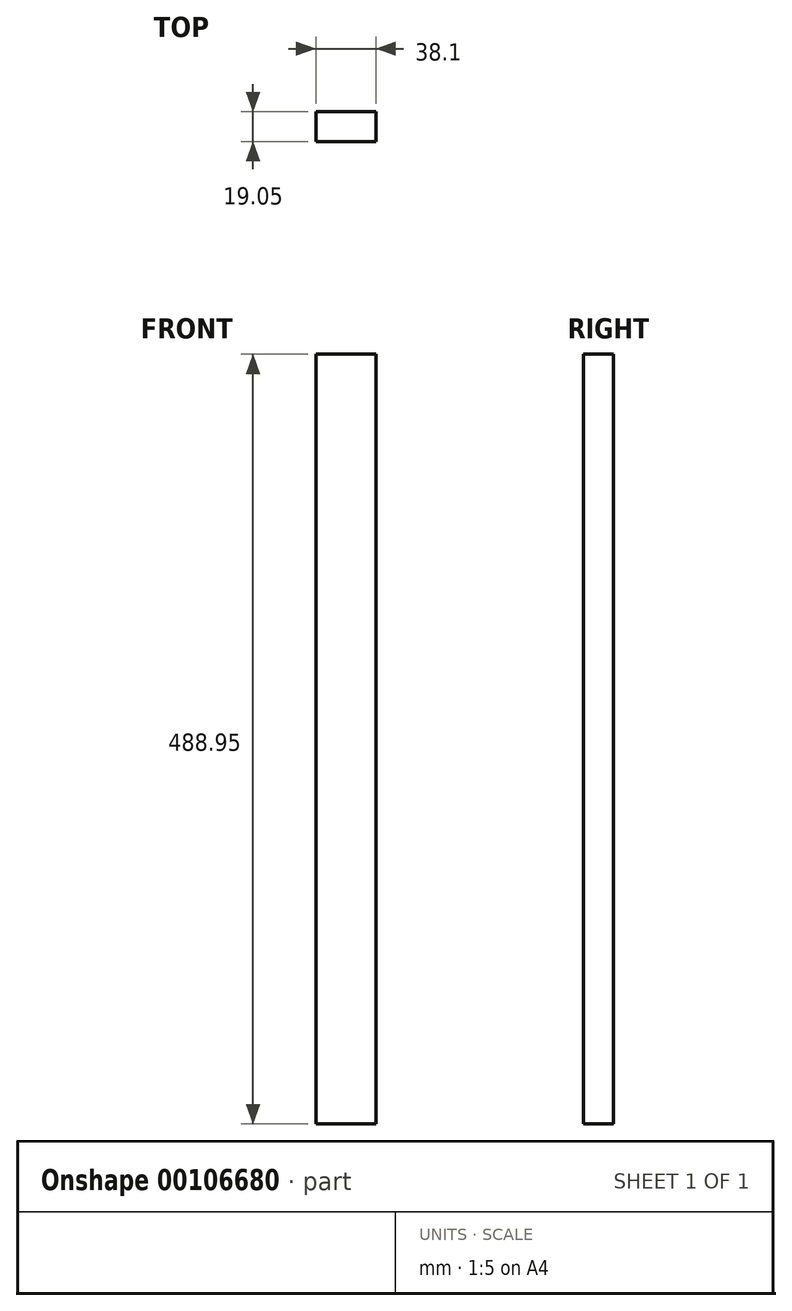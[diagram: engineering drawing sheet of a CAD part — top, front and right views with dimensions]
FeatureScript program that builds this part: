
annotation { "Feature Type Name" : "Feature", "Feature Type Description" : "" }
export const myFeature = defineFeature(function(context is Context, id is Id, definition is map)
    precondition{}
    {
        {
            var Q0;
            Q0=qCreatedBy(makeId("Front.planeOp"),FACE);
            var sketch = newSketch(context, id + "F0", { "sketchPlane" : qUnion([Q0])});
            skLineSegment(sketch, "E0.bottom", {"start": v(0, 0) * mm, "end": v(38.1, 0) * mm});
            skLineSegment(sketch, "E0.left", {"start": v(0, 0) * mm, "end": v(0, 488.95) * mm});
            skLineSegment(sketch, "E0.right", {"start": v(38.1, 0) * mm, "end": v(38.1, 488.95) * mm});
            skLineSegment(sketch, "E1", {"start": v(0, 488.95) * mm, "end": v(38.1, 488.95) * mm});
            skSolve(sketch);
        }
        {
            var Q0;
            Q0=makeQuery(id+"F0.imprint","IMPRINT",FACE,{"disambiguationData":[TD([[makeQuery(id+"F0.imprint","IMPRINT",EDGE,{"derivedFrom":sQuery(id+"F0.wireOp",EDGE,"E0.bottom")}),1.0]])]});
            extrude(context, id + "F1", {"entities" : qUnion([Q0]), "depth" : 19.05 * mm});
        }
    });
